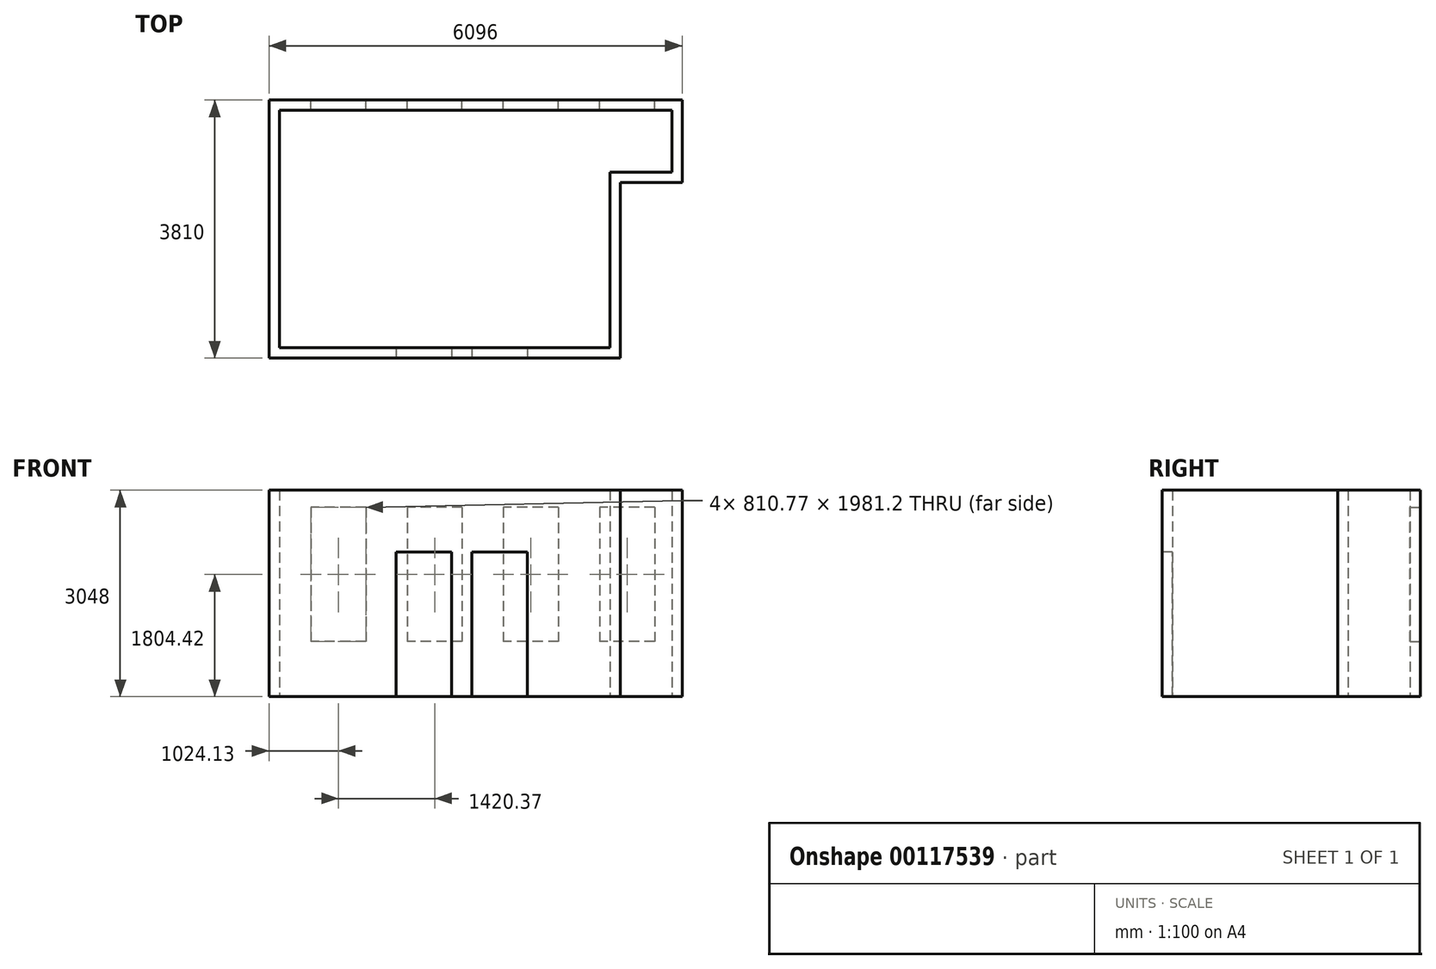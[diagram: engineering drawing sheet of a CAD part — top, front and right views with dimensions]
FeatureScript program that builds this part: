
annotation { "Feature Type Name" : "Feature", "Feature Type Description" : "" }
export const myFeature = defineFeature(function(context is Context, id is Id, definition is map)
    precondition{}
    {
        {
            var Q0;
            Q0=qCreatedBy(makeId("Top.planeOp"),FACE);
            var sketch = newSketch(context, id + "F0", { "sketchPlane" : qUnion([Q0])});
            skLineSegment(sketch, "E0.bottom", {"start": v(-2652.48, 1933.51) * mm, "end": v(3138.72, 1933.51) * mm});
            skLineSegment(sketch, "E0.top", {"start": v(-2652.48, -1571.69) * mm, "end": v(2224.32, -1571.69) * mm});
            skLineSegment(sketch, "E0.left", {"start": v(-2652.48, 1933.51) * mm, "end": v(-2652.48, -1571.69) * mm});
            skLineSegment(sketch, "E0.right", {"start": v(2224.32, 1019.11) * mm, "end": v(2224.32, -1571.69) * mm});
            skLineSegment(sketch, "E1.top", {"start": v(2224.32, 1019.11) * mm, "end": v(3138.72, 1019.11) * mm});
            skLineSegment(sketch, "E1.right", {"start": v(3138.72, 1933.51) * mm, "end": v(3138.72, 1019.11) * mm});
            skLineSegment(sketch, "E2", {"start": v(-2804.88, -1724.09) * mm, "end": v(-2804.88, 2085.91) * mm});
            skLineSegment(sketch, "E3", {"start": v(-2804.88, 2085.91) * mm, "end": v(3291.12, 2085.91) * mm});
            skLineSegment(sketch, "E4", {"start": v(2376.72, 866.71) * mm, "end": v(2376.72, -1724.09) * mm});
            skLineSegment(sketch, "E5", {"start": v(2376.72, -1724.09) * mm, "end": v(-2804.88, -1724.09) * mm});
            skLineSegment(sketch, "E6", {"start": v(3291.12, 2085.91) * mm, "end": v(3291.12, 866.71) * mm});
            skLineSegment(sketch, "E7", {"start": v(3291.12, 866.71) * mm, "end": v(2376.72, 866.71) * mm});
            skSolve(sketch);
        }
        {
            var Q0;
            Q0=makeQuery(id+"F0.imprint","IMPRINT",FACE,{"disambiguationData":[TD([[makeQuery(id+"F0.imprint","IMPRINT",EDGE,{"derivedFrom":sQuery(id+"F0.wireOp",EDGE,"E0.bottom")}),1.0]])]});
            extrude(context, id + "F1", {"entities" : qUnion([Q0]), "depth" : 3048 * mm});
        }
        {
            var Q0;
            Q0=makeQuery(id+"F1.opExtrude","SWEPT_FACE",FACE,{"disambiguationData":[OSD([sQuery(id+"F0.wireOp",EDGE,"E5")])]});
            var sketch = newSketch(context, id + "F2", { "sketchPlane" : qUnion([Q0])});
            skLineSegment(sketch, "E8.bottom", {"start": v(1005.12, 0) * mm, "end": v(191.3, 0) * mm});
            skLineSegment(sketch, "E8.top", {"start": v(1005.12, 2133.6) * mm, "end": v(191.3, 2133.6) * mm});
            skLineSegment(sketch, "E8.left", {"start": v(1005.12, 0) * mm, "end": v(1005.12, 2133.6) * mm});
            skLineSegment(sketch, "E8.right", {"start": v(191.3, 0) * mm, "end": v(191.3, 2133.6) * mm});
            skLineSegment(sketch, "E9.bottom", {"start": v(-113.5, 0) * mm, "end": v(-927.31, 0) * mm});
            skLineSegment(sketch, "E9.top", {"start": v(-113.5, 2133.6) * mm, "end": v(-927.31, 2133.6) * mm});
            skLineSegment(sketch, "E9.left", {"start": v(-113.5, 0) * mm, "end": v(-113.5, 2133.6) * mm});
            skLineSegment(sketch, "E9.right", {"start": v(-927.31, 0) * mm, "end": v(-927.31, 2133.6) * mm});
            skSolve(sketch);
        }
        {
            var Q0;
            Q0=makeQuery(id+"F2.imprint","IMPRINT",FACE,{"disambiguationData":[TD([[makeQuery(id+"F2.imprint","IMPRINT",EDGE,{"derivedFrom":sQuery(id+"F2.wireOp",EDGE,"E9.bottom")}),-1.0]])]});
            var Q1;
            Q1=makeQuery(id+"F2.imprint","IMPRINT",FACE,{"disambiguationData":[TD([[makeQuery(id+"F2.imprint","IMPRINT",EDGE,{"derivedFrom":sQuery(id+"F2.wireOp",EDGE,"E8.bottom")}),-1.0]])]});
            var Q2;
            Q2=makeQuery(id+"F1.opExtrude","SWEPT_FACE",FACE,{"disambiguationData":[OSD([sQuery(id+"F0.wireOp",EDGE,"E0.top")])]});
            extrude(context, id + "F3", {"entities" : qUnion([Q0, Q1]), "operationType" : NewBodyOperationType.REMOVE, "endBound" : BoundingType.UP_TO_SURFACE, "oppositeDirection" : true, "endBoundEntityFace" : qUnion([Q2]), "depth" : 30.48 * mm});
        }
        {
            var Q0;
            Q0=makeQuery(id+"F1.opExtrude","SWEPT_FACE",FACE,{"disambiguationData":[OSD([sQuery(id+"F0.wireOp",EDGE,"E3")])]});
            var sketch = newSketch(context, id + "F4", { "sketchPlane" : qUnion([Q0])});
            skLineSegment(sketch, "E10.bottom", {"start": v(-2885.74, 2795.02) * mm, "end": v(-2074.97, 2795.02) * mm});
            skLineSegment(sketch, "E10.top", {"start": v(-2885.74, 813.82) * mm, "end": v(-2074.97, 813.82) * mm});
            skLineSegment(sketch, "E10.left", {"start": v(-2885.74, 2795.02) * mm, "end": v(-2885.74, 813.82) * mm});
            skLineSegment(sketch, "E10.right", {"start": v(-2074.97, 2795.02) * mm, "end": v(-2074.97, 813.82) * mm});
            skLineSegment(sketch, "E11.bottom", {"start": v(-1465.37, 2795.02) * mm, "end": v(-654.6, 2795.02) * mm});
            skLineSegment(sketch, "E11.top", {"start": v(-1465.37, 813.82) * mm, "end": v(-654.6, 813.82) * mm});
            skLineSegment(sketch, "E11.left", {"start": v(-1465.37, 2795.02) * mm, "end": v(-1465.37, 813.82) * mm});
            skLineSegment(sketch, "E11.right", {"start": v(-654.6, 2795.02) * mm, "end": v(-654.6, 813.82) * mm});
            skLineSegment(sketch, "E12.bottom", {"start": v(-45, 2795.02) * mm, "end": v(765.77, 2795.02) * mm});
            skLineSegment(sketch, "E12.top", {"start": v(-45, 813.82) * mm, "end": v(765.77, 813.82) * mm});
            skLineSegment(sketch, "E12.left", {"start": v(-45, 2795.02) * mm, "end": v(-45, 813.82) * mm});
            skLineSegment(sketch, "E12.right", {"start": v(765.77, 2795.02) * mm, "end": v(765.77, 813.82) * mm});
            skLineSegment(sketch, "E13.bottom", {"start": v(1375.37, 2795.02) * mm, "end": v(2186.14, 2795.02) * mm});
            skLineSegment(sketch, "E13.top", {"start": v(1375.37, 813.82) * mm, "end": v(2186.14, 813.82) * mm});
            skLineSegment(sketch, "E13.left", {"start": v(1375.37, 2795.02) * mm, "end": v(1375.37, 813.82) * mm});
            skLineSegment(sketch, "E13.right", {"start": v(2186.14, 2795.02) * mm, "end": v(2186.14, 813.82) * mm});
            skLineSegment(sketch, "E14", {"start": v(-4137.53, 813.82) * mm, "end": v(3423.56, 813.82) * mm, "construction": true});
            skLineSegment(sketch, "E15", {"start": v(-2074.97, 2795.02) * mm, "end": v(-1465.37, 2795.02) * mm, "construction": true});
            skLineSegment(sketch, "E16", {"start": v(-654.6, 2795.02) * mm, "end": v(-45, 2795.02) * mm, "construction": true});
            skLineSegment(sketch, "E17", {"start": v(765.77, 2795.02) * mm, "end": v(1375.37, 2795.02) * mm, "construction": true});
            skSolve(sketch);
        }
        {
            var Q0;
            Q0=makeQuery(id+"F4.imprint","IMPRINT",FACE,{"disambiguationData":[TD([[makeQuery(id+"F4.imprint","IMPRINT",EDGE,{"derivedFrom":sQuery(id+"F4.wireOp",EDGE,"E10.bottom")}),-1.0]])]});
            var Q1;
            Q1=makeQuery(id+"F4.imprint","IMPRINT",FACE,{"disambiguationData":[TD([[makeQuery(id+"F4.imprint","IMPRINT",EDGE,{"derivedFrom":sQuery(id+"F4.wireOp",EDGE,"E11.bottom")}),-1.0]])]});
            var Q2;
            Q2=makeQuery(id+"F4.imprint","IMPRINT",FACE,{"disambiguationData":[TD([[makeQuery(id+"F4.imprint","IMPRINT",EDGE,{"derivedFrom":sQuery(id+"F4.wireOp",EDGE,"E12.bottom")}),-1.0]])]});
            var Q3;
            Q3=makeQuery(id+"F4.imprint","IMPRINT",FACE,{"disambiguationData":[TD([[makeQuery(id+"F4.imprint","IMPRINT",EDGE,{"derivedFrom":sQuery(id+"F4.wireOp",EDGE,"E13.bottom")}),-1.0]])]});
            var Q4;
            Q4=makeQuery(id+"F1.opExtrude","SWEPT_FACE",FACE,{"disambiguationData":[OSD([sQuery(id+"F0.wireOp",EDGE,"E0.bottom")])]});
            extrude(context, id + "F5", {"entities" : qUnion([Q0, Q1, Q2, Q3]), "operationType" : NewBodyOperationType.REMOVE, "endBound" : BoundingType.UP_TO_SURFACE, "oppositeDirection" : true, "endBoundEntityFace" : qUnion([Q4]), "depth" : 30.48 * mm});
        }
        {
            var Q0;
            Q0=makeQuery(id+"F1.opExtrude","SWEPT_FACE",FACE,{"disambiguationData":[OSD([sQuery(id+"F0.wireOp",EDGE,"E5")])]});
            var sketch = newSketch(context, id + "F6", { "sketchPlane" : qUnion([Q0])});
            skLineSegment(sketch, "E18.bottom", {"start": v(-927.31, 2133.6) * mm, "end": v(-113.5, 2133.6) * mm});
            skLineSegment(sketch, "E18.top", {"start": v(-927.31, 0) * mm, "end": v(-113.5, 0) * mm});
            skLineSegment(sketch, "E18.left", {"start": v(-927.31, 2133.6) * mm, "end": v(-927.31, 0) * mm});
            skLineSegment(sketch, "E18.right", {"start": v(-113.5, 2133.6) * mm, "end": v(-113.5, 0) * mm});
            skLineSegment(sketch, "E19.bottom", {"start": v(191.3, 2133.6) * mm, "end": v(1005.12, 2133.6) * mm});
            skLineSegment(sketch, "E19.top", {"start": v(191.3, 0) * mm, "end": v(1005.12, 0) * mm});
            skLineSegment(sketch, "E19.left", {"start": v(191.3, 2133.6) * mm, "end": v(191.3, 0) * mm});
            skLineSegment(sketch, "E19.right", {"start": v(1005.12, 2133.6) * mm, "end": v(1005.12, 0) * mm});
            skSolve(sketch);
        }
        {
            var Q0;
            Q0 = qSketchRegion(id + "F6", true);
            extrude(context, id + "F7", {"entities" : qUnion([Q0]), "depth" : 1 / 1828.8 * mm});
        }
    });
